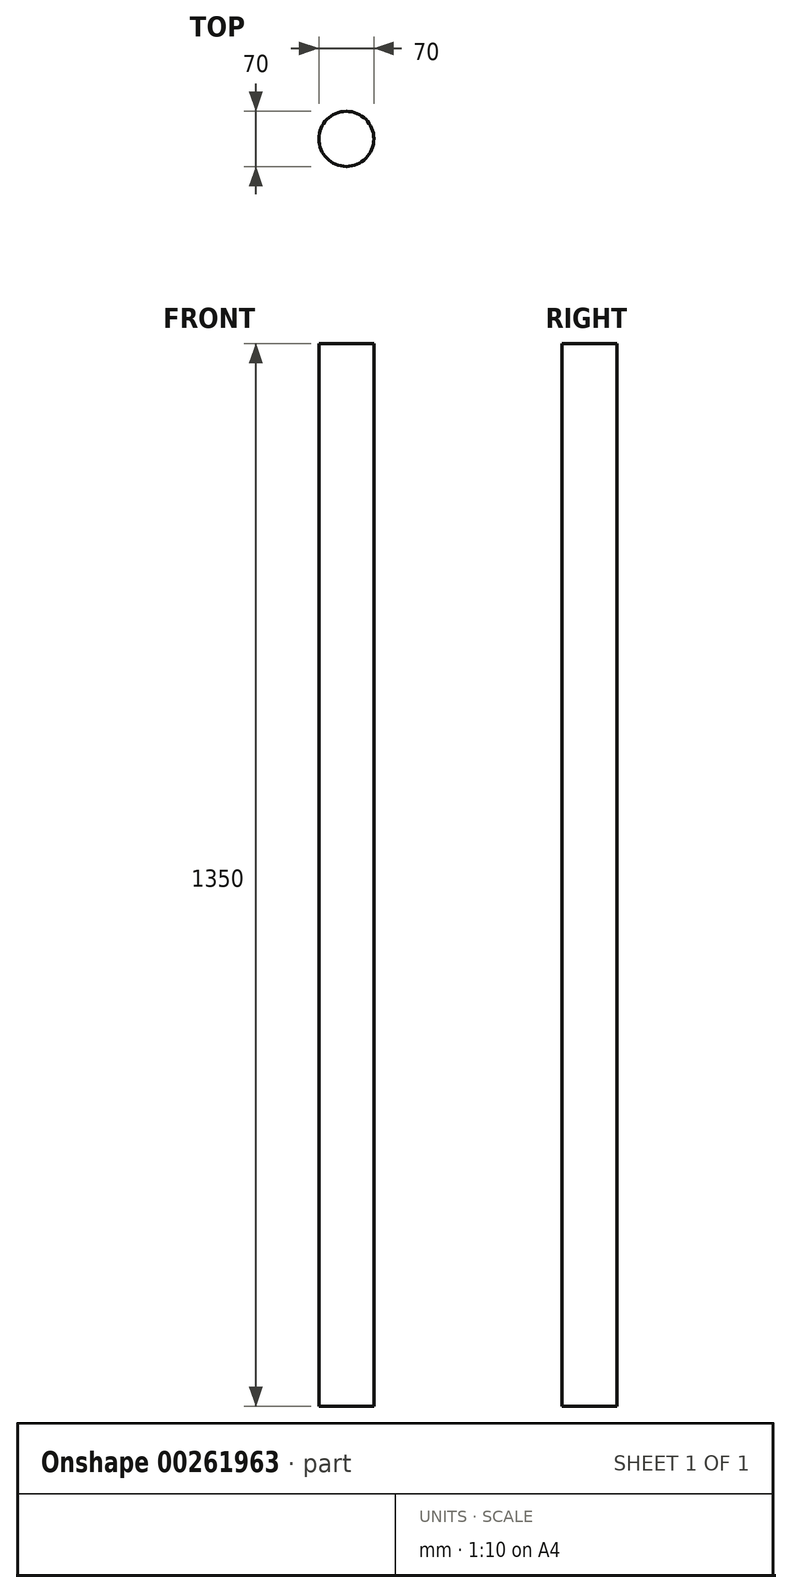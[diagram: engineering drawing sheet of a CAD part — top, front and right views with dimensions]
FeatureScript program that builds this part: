
annotation { "Feature Type Name" : "Feature", "Feature Type Description" : "" }
export const myFeature = defineFeature(function(context is Context, id is Id, definition is map)
    precondition{}
    {
        {
            var Q0;
            Q0=qCreatedBy(makeId("Top.planeOp"), FACE);
            var sketch = newSketch(context, id + "F0", { "sketchPlane" : qUnion([Q0])});
            skCircle(sketch, "E0", {"center": v(-65.08, 30.97) * mm, "radius": 35 * mm});
            skSolve(sketch);
        }
        {
            var Q0;
            Q0 = qSketchRegion(id + "F0", true);
            extrude(context, id + "F1", {"entities" : qUnion([Q0]), "depth" : 1350 * mm, "offsetDistance" : 25 * mm});
        }
    });
